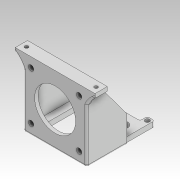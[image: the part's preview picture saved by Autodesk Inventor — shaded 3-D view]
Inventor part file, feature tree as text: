
AUTODESK INVENTOR PART (.ipt)
format: ipt  version: 2020 (Build 240168000, 168)  size: 327,168 bytes
history: native  units: mm
features: extrude x10, sketch x10, fillet x4, mirror x2, plane x1, chamfer x1, projected_geometry x1
ambient origin geometry x8: Origin, YZ Plane, XZ Plane, XY Plane, X Axis, Y Axis, Z Axis, Center Point
bodies: Solid1 (feature_tree)
feature tree (29):
  extrude  "Extrusion1"  Depth=47.0mm
  extrude  "Extrusion2"  Depth=40.0mm
  extrude  "Extrusion3"  Depth=3.5mm TaperAngle=0.0deg
  extrude  "Extrusion4"  Depth=10.0mm
  mirror  "Mirror1"
  fillet  "Fillet1"  Radius=4.0mm
  extrude  "Extrusion5"  TaperAngle=0.0deg  [1 undecoded]
  plane  "Work Plane1"
  extrude  "Extrusion6"  Depth=25.0mm
  extrude  "Extrusion7"  Depth=5.0mm
  extrude  "Extrusion8"  TaperAngle=0.0deg  [1 undecoded]
  extrude  "Extrusion9"  Depth=10.0mm TaperAngle=0.0deg
  chamfer  "Chamfer2"  Distance=7.0mm
  mirror  "Mirror2"
  fillet  "Fillet2"  Radius=7.0mm
  fillet  "Fillet3"  Radius=7.2mm
  fillet  "Fillet4"  Radius=7.0mm
  extrude  "Extrusion10"  Depth=10.0mm TaperAngle=0.0deg
  sketch  "Sketch1"  dims[d0=5.2mm d1=47.0mm]
  sketch  "Sketch2"  dims[d2=47.0mm d3=40.0mm]
  projected_geometry  "Projected Loop1"
  sketch  "Sketch3"  dims[d4=58.0mm d5=3.5mm d6=0.0mm]
  sketch  "Sketch4"  dims[d7=10.0mm d8=12.0mm d9=4.0mm d10=0.0mm]
  sketch  "Sketch5"  dims[d15=4.0mm d16=0.0mm d18=0.0mm d19=0.0mm]
  sketch  "Sketch6"  dims[d20=45.0deg d21=25.0mm]
  sketch  "Sketch7"  dims[d22=5.0mm d23=5.0mm]
  sketch  "Sketch8"  dims[d24=3.3mm d25=0.0mm d26=0.0mm]
  sketch  "Sketch9"  dims[d27=6.0mm d28=10.0mm d29=0.0mm]
  sketch  "Sketch10"  dims[d30=-6.5mm d32=7.0mm d33=7.0mm d35=7.2mm d36=7.0mm d37=5.0mm d38=0.0mm d39=61.0mm d40=5.0mm d41=7.0mm d42=3.5mm d43=4.3mm d44=5.0mm d45=0.0mm d46=2.0mm d47=2.0mm d50=2.0mm d51=0.0mm d52=1.0mm d53=2.0mm d54=45.0deg d55=2.0mm d56=55.0mm d57=15.0mm d58=10.0mm d59=0.0mm]
note: 2 required parameter values undecoded (feature->parameter linkage not recoverable at this tier; creation-order binding heuristic only, values carry confidence <= 0.55)
